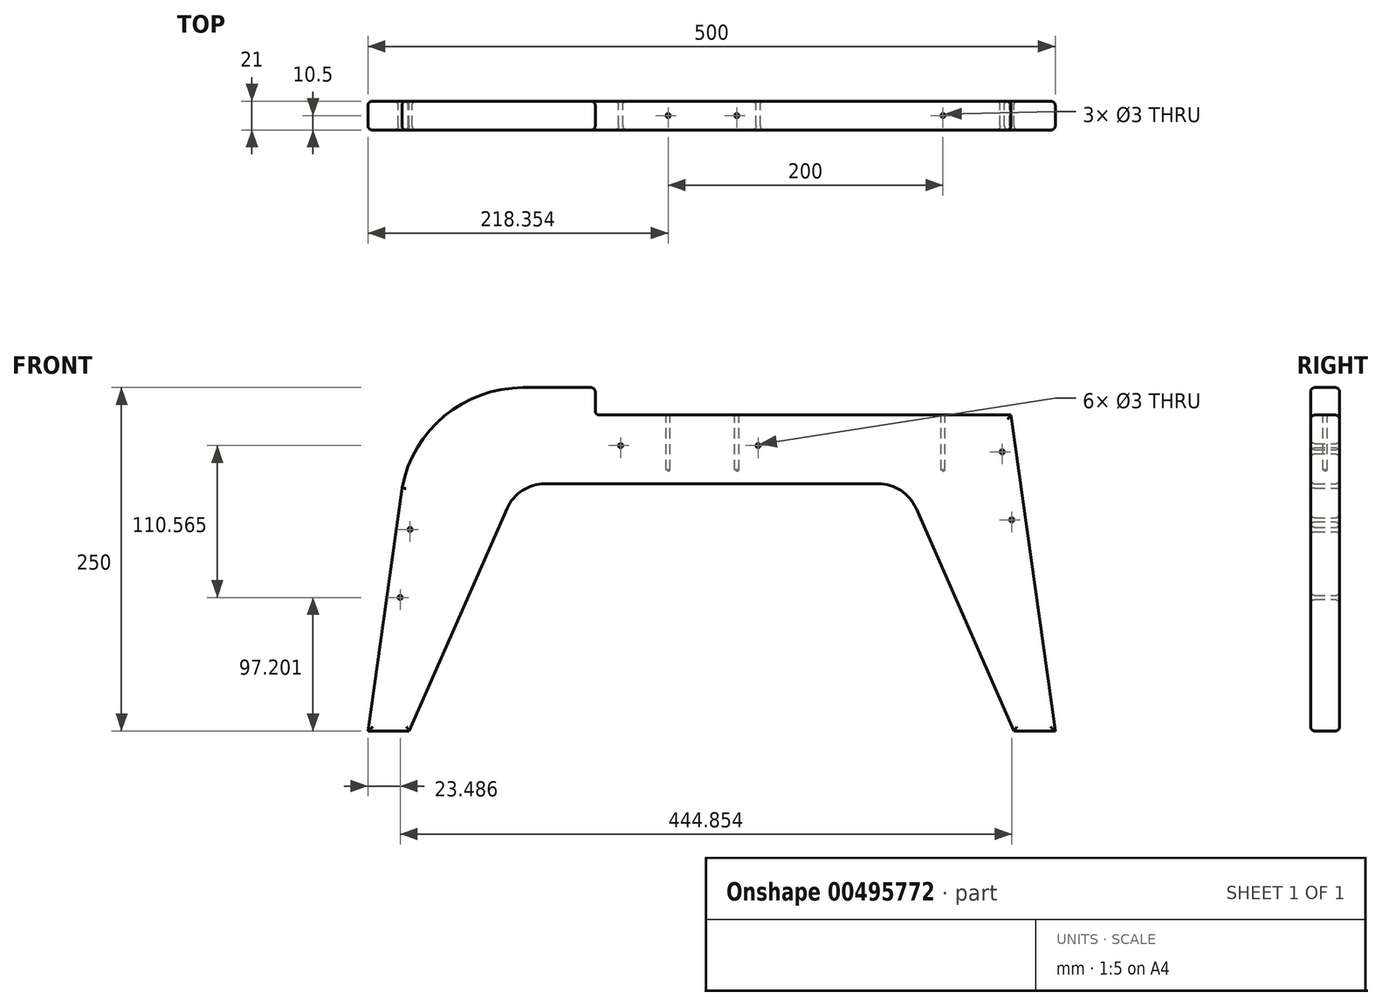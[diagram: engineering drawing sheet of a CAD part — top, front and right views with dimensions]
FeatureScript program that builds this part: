
annotation { "Feature Type Name" : "Feature", "Feature Type Description" : "" }
export const myFeature = defineFeature(function(context is Context, id is Id, definition is map)
    precondition{}
    {
        {
            var Q0;
            Q0=qCreatedBy(makeId("Front.planeOp"),FACE);
            var sketch = newSketch(context, id + "F0", { "sketchPlane" : qUnion([Q0])});
            skLineSegment(sketch, "E0.bottom", {"start": v(-250, -242.11) * mm, "end": v(-220, -242.11) * mm});
            skLineSegment(sketch, "E1", {"start": v(220, -242.11) * mm, "end": v(250, -242.11) * mm});
            skLineSegment(sketch, "E2", {"start": v(-220, -242.11) * mm, "end": v(-148.68, -80.03) * mm});
            skLineSegment(sketch, "E3", {"start": v(220, -242.11) * mm, "end": v(148.68, -80.03) * mm});
            skLineSegment(sketch, "E4", {"start": v(110, 7.89) * mm, "end": v(110, 7.89) * mm});
            skLineSegment(sketch, "E5", {"start": v(-121.22, -62.11) * mm, "end": v(121.22, -62.11) * mm});
            skLineSegment(sketch, "E6", {"start": v(217.8, -12.11) * mm, "end": v(250, -242.11) * mm});
            skPoint(sketch, "E7.end.orphan", {"position": v(110, 7.89) * mm});
            skPoint(sketch, "E8.visualSharp", {"position": v(-140.8, -62.11) * mm});
            skArc(sketch, "E8.filletArc", {"start": v(-121.22, -62.11) * mm, "mid": v(-137.62, -66.99) * mm, "end": v(-148.68, -80.03) * mm});
            skPoint(sketch, "E9.visualSharp", {"position": v(140.8, -62.11) * mm});
            skArc(sketch, "E9.filletArc", {"start": v(148.68, -80.03) * mm, "mid": v(137.62, -66.99) * mm, "end": v(121.22, -62.11) * mm});
            skLineSegment(sketch, "E10", {"start": v(-225.23, -65.16) * mm, "end": v(-250, -242.11) * mm});
            skLineSegment(sketch, "E11", {"start": v(-110, 7.89) * mm, "end": v(-137.11, 7.89) * mm});
            skArc(sketch, "E12", {"start": v(-137.11, 7.89) * mm, "mid": v(-194.34, -12.75) * mm, "end": v(-225.23, -65.16) * mm});
            skLineSegment(sketch, "E13", {"start": v(-74.6, -12.11) * mm, "end": v(217.8, -12.11) * mm});
            skLineSegment(sketch, "E14", {"start": v(-81.65, -12.11) * mm, "end": v(-74.6, -12.11) * mm});
            skLineSegment(sketch, "E15", {"start": v(-84.65, 4.89) * mm, "end": v(-84.65, -9.11) * mm});
            skLineSegment(sketch, "E16", {"start": v(-110, 7.89) * mm, "end": v(-87.65, 7.89) * mm});
            skPoint(sketch, "E17.visualSharp", {"position": v(-84.65, -12.11) * mm});
            skArc(sketch, "E17.filletArc", {"start": v(-84.65, -9.11) * mm, "mid": v(-83.77, -11.23) * mm, "end": v(-81.65, -12.11) * mm});
            skPoint(sketch, "E18.visualSharp", {"position": v(-84.65, 7.89) * mm});
            skArc(sketch, "E18.filletArc", {"start": v(-84.65, 4.89) * mm, "mid": v(-85.53, 7) * mm, "end": v(-87.65, 7.89) * mm});
            skCircle(sketch, "E19", {"center": v(-66.17, -34.35) * mm, "radius": 1.5 * mm});
            skCircle(sketch, "E20", {"center": v(33.83, -34.35) * mm, "radius": 1.5 * mm});
            skCircle(sketch, "E21", {"center": v(211.4, -38.85) * mm, "radius": 1.5 * mm});
            skCircle(sketch, "E22", {"center": v(218.34, -88.37) * mm, "radius": 1.5 * mm});
            skCircle(sketch, "E23", {"center": v(-226.51, -144.9) * mm, "radius": 1.5 * mm});
            skCircle(sketch, "E24", {"center": v(-219.37, -95.42) * mm, "radius": 1.5 * mm});
            skSolve(sketch);
        }
        {
            var Q0;
            Q0=makeQuery(id+"F0.imprint","IMPRINT",FACE,{"disambiguationData":[TD([[makeQuery(id+"F0.imprint","IMPRINT",EDGE,{"derivedFrom":sQuery(id+"F0.wireOp",EDGE,"E0.bottom")}),1.0]])]});
            extrude(context, id + "F1", {"entities" : qUnion([Q0]), "endBound" : BoundingType.SYMMETRIC, "depth" : 21 * mm});
        }
        {
            var Q0;
            Q0=makeQuery(id+"F1.opExtrude","CAP_FACE",FACE,{"disambiguationData":[OSD([sQuery(id+"F0.wireOp",EDGE,"E0.bottom"),sQuery(id+"F0.wireOp",EDGE,"E1"),sQuery(id+"F0.wireOp",EDGE,"E2"),sQuery(id+"F0.wireOp",EDGE,"E3"),sQuery(id+"F0.wireOp",EDGE,"E5"),sQuery(id+"F0.wireOp",EDGE,"E6"),sQuery(id+"F0.wireOp",EDGE,"E8.filletArc"),sQuery(id+"F0.wireOp",EDGE,"E9.filletArc"),sQuery(id+"F0.wireOp",EDGE,"E10"),sQuery(id+"F0.wireOp",EDGE,"E11"),sQuery(id+"F0.wireOp",EDGE,"E12"),sQuery(id+"F0.wireOp",EDGE,"E13"),sQuery(id+"F0.wireOp",EDGE,"E14"),sQuery(id+"F0.wireOp",EDGE,"E15"),sQuery(id+"F0.wireOp",EDGE,"E16"),sQuery(id+"F0.wireOp",EDGE,"E17.filletArc"),sQuery(id+"F0.wireOp",EDGE,"E18.filletArc"),sQuery(id+"F0.wireOp",EDGE,"E19"),sQuery(id+"F0.wireOp",EDGE,"E20"),sQuery(id+"F0.wireOp",EDGE,"E21"),sQuery(id+"F0.wireOp",EDGE,"E22"),sQuery(id+"F0.wireOp",EDGE,"E23"),sQuery(id+"F0.wireOp",EDGE,"E24")])],"isStart":false});
            var Q1;
            Q1=makeQuery(id+"F1.opExtrude","CAP_EDGE",EDGE,{"disambiguationData":[OSD([sQuery(id+"F0.wireOp",EDGE,"E2")])],"isStart":false});
            var Q2;
            Q2=makeQuery(id+"F1.opExtrude","CAP_EDGE",EDGE,{"disambiguationData":[OSD([sQuery(id+"F0.wireOp",EDGE,"E2")])],"isStart":true});
            var Q3;
            Q3=makeQuery(id+"F1.opExtrude","CAP_FACE",FACE,{"disambiguationData":[OSD([sQuery(id+"F0.wireOp",EDGE,"E0.bottom"),sQuery(id+"F0.wireOp",EDGE,"E1"),sQuery(id+"F0.wireOp",EDGE,"E2"),sQuery(id+"F0.wireOp",EDGE,"E3"),sQuery(id+"F0.wireOp",EDGE,"E5"),sQuery(id+"F0.wireOp",EDGE,"E6"),sQuery(id+"F0.wireOp",EDGE,"E8.filletArc"),sQuery(id+"F0.wireOp",EDGE,"E9.filletArc"),sQuery(id+"F0.wireOp",EDGE,"E10"),sQuery(id+"F0.wireOp",EDGE,"E11"),sQuery(id+"F0.wireOp",EDGE,"E12"),sQuery(id+"F0.wireOp",EDGE,"E13"),sQuery(id+"F0.wireOp",EDGE,"E14"),sQuery(id+"F0.wireOp",EDGE,"E15"),sQuery(id+"F0.wireOp",EDGE,"E16"),sQuery(id+"F0.wireOp",EDGE,"E17.filletArc"),sQuery(id+"F0.wireOp",EDGE,"E18.filletArc"),sQuery(id+"F0.wireOp",EDGE,"E19"),sQuery(id+"F0.wireOp",EDGE,"E20"),sQuery(id+"F0.wireOp",EDGE,"E21"),sQuery(id+"F0.wireOp",EDGE,"E22"),sQuery(id+"F0.wireOp",EDGE,"E23"),sQuery(id+"F0.wireOp",EDGE,"E24")])],"isStart":true});
            fillet(context, id + "F2", {"entities" : qUnion([Q0, Q1, Q2, Q3]), "radius" : 3 * mm, "tangentPropagation" : true, "allowEdgeOverflow" : false});
        }
        {
            var Q0;
            Q0=makeQuery(id+"F1.opExtrude","SWEPT_FACE",FACE,{"disambiguationData":[OSD([sQuery(id+"F0.wireOp",EDGE,"E13"),sQuery(id+"F0.wireOp",EDGE,"E14")])]});
            var sketch = newSketch(context, id + "F3", { "sketchPlane" : qUnion([Q0])});
            skLineSegment(sketch, "E25", {"start": v(-81.65, 0) * mm, "end": v(-31.65, 0) * mm});
            skLineSegment(sketch, "E26", {"start": v(-31.65, 0) * mm, "end": v(18.35, 0) * mm});
            skLineSegment(sketch, "E27", {"start": v(168.35, 0) * mm, "end": v(217.8, 0) * mm});
            skLineSegment(sketch, "E28", {"start": v(18.35, 0) * mm, "end": v(168.35, 0) * mm});
            skSolve(sketch);
        }
        {
            var Q0;
            Q0=sQuery(id+"F3.wireOp",VERTEX,"E26.start");
            var Q1;
            Q1=makeQuery(id+"F1.opExtrude","SWEPT_BODY",BODY,{"disambiguationData":[OSD([sQuery(id+"F0.wireOp",EDGE,"E0.bottom"),sQuery(id+"F0.wireOp",EDGE,"E1"),sQuery(id+"F0.wireOp",EDGE,"E2"),sQuery(id+"F0.wireOp",EDGE,"E3"),sQuery(id+"F0.wireOp",EDGE,"E5"),sQuery(id+"F0.wireOp",EDGE,"E6"),sQuery(id+"F0.wireOp",EDGE,"E8.filletArc"),sQuery(id+"F0.wireOp",EDGE,"E9.filletArc"),sQuery(id+"F0.wireOp",EDGE,"E10"),sQuery(id+"F0.wireOp",EDGE,"E11"),sQuery(id+"F0.wireOp",EDGE,"E12"),sQuery(id+"F0.wireOp",EDGE,"E13"),sQuery(id+"F0.wireOp",EDGE,"E14"),sQuery(id+"F0.wireOp",EDGE,"E15"),sQuery(id+"F0.wireOp",EDGE,"E16"),sQuery(id+"F0.wireOp",EDGE,"E17.filletArc"),sQuery(id+"F0.wireOp",EDGE,"E18.filletArc"),sQuery(id+"F0.wireOp",EDGE,"E19"),sQuery(id+"F0.wireOp",EDGE,"E20"),sQuery(id+"F0.wireOp",EDGE,"E21"),sQuery(id+"F0.wireOp",EDGE,"E22"),sQuery(id+"F0.wireOp",EDGE,"E23"),sQuery(id+"F0.wireOp",EDGE,"E24")])]});
            hole(context, id + "F4", {"style" : HoleStyle.SIMPLE, "endStyle" : HoleEndStyle.BLIND, "holeDiameter" : 3 * mm, "holeDepth" : 40 * mm, "isTappedThrough" : true, "tappedDepth" : 12 * mm, "tapClearance" : 3, "locations" : qUnion([Q0]), "scope" : qUnion([Q1])});
        }
        {
            var Q0;
            Q0=sQuery(id+"F3.wireOp",VERTEX,"E28.start");
            var Q1;
            Q1=makeQuery(id+"F1.opExtrude","SWEPT_BODY",BODY,{"disambiguationData":[OSD([sQuery(id+"F0.wireOp",EDGE,"E0.bottom"),sQuery(id+"F0.wireOp",EDGE,"E1"),sQuery(id+"F0.wireOp",EDGE,"E2"),sQuery(id+"F0.wireOp",EDGE,"E3"),sQuery(id+"F0.wireOp",EDGE,"E5"),sQuery(id+"F0.wireOp",EDGE,"E6"),sQuery(id+"F0.wireOp",EDGE,"E8.filletArc"),sQuery(id+"F0.wireOp",EDGE,"E9.filletArc"),sQuery(id+"F0.wireOp",EDGE,"E10"),sQuery(id+"F0.wireOp",EDGE,"E11"),sQuery(id+"F0.wireOp",EDGE,"E12"),sQuery(id+"F0.wireOp",EDGE,"E13"),sQuery(id+"F0.wireOp",EDGE,"E14"),sQuery(id+"F0.wireOp",EDGE,"E15"),sQuery(id+"F0.wireOp",EDGE,"E16"),sQuery(id+"F0.wireOp",EDGE,"E17.filletArc"),sQuery(id+"F0.wireOp",EDGE,"E18.filletArc"),sQuery(id+"F0.wireOp",EDGE,"E19"),sQuery(id+"F0.wireOp",EDGE,"E20"),sQuery(id+"F0.wireOp",EDGE,"E21"),sQuery(id+"F0.wireOp",EDGE,"E22"),sQuery(id+"F0.wireOp",EDGE,"E23"),sQuery(id+"F0.wireOp",EDGE,"E24")])]});
            hole(context, id + "F5", {"style" : HoleStyle.SIMPLE, "endStyle" : HoleEndStyle.BLIND, "holeDiameter" : 3 * mm, "holeDepth" : 40 * mm, "isTappedThrough" : true, "tappedDepth" : 12 * mm, "tapClearance" : 3, "locations" : qUnion([Q0]), "scope" : qUnion([Q1])});
        }
        {
            var Q0;
            Q0=sQuery(id+"F3.wireOp",VERTEX,"E28.end");
            var Q1;
            Q1=makeQuery(id+"F1.opExtrude","SWEPT_BODY",BODY,{"disambiguationData":[OSD([sQuery(id+"F0.wireOp",EDGE,"E0.bottom"),sQuery(id+"F0.wireOp",EDGE,"E1"),sQuery(id+"F0.wireOp",EDGE,"E2"),sQuery(id+"F0.wireOp",EDGE,"E3"),sQuery(id+"F0.wireOp",EDGE,"E5"),sQuery(id+"F0.wireOp",EDGE,"E6"),sQuery(id+"F0.wireOp",EDGE,"E8.filletArc"),sQuery(id+"F0.wireOp",EDGE,"E9.filletArc"),sQuery(id+"F0.wireOp",EDGE,"E10"),sQuery(id+"F0.wireOp",EDGE,"E11"),sQuery(id+"F0.wireOp",EDGE,"E12"),sQuery(id+"F0.wireOp",EDGE,"E13"),sQuery(id+"F0.wireOp",EDGE,"E14"),sQuery(id+"F0.wireOp",EDGE,"E15"),sQuery(id+"F0.wireOp",EDGE,"E16"),sQuery(id+"F0.wireOp",EDGE,"E17.filletArc"),sQuery(id+"F0.wireOp",EDGE,"E18.filletArc"),sQuery(id+"F0.wireOp",EDGE,"E19"),sQuery(id+"F0.wireOp",EDGE,"E20"),sQuery(id+"F0.wireOp",EDGE,"E21"),sQuery(id+"F0.wireOp",EDGE,"E22"),sQuery(id+"F0.wireOp",EDGE,"E23"),sQuery(id+"F0.wireOp",EDGE,"E24")])]});
            hole(context, id + "F6", {"style" : HoleStyle.SIMPLE, "endStyle" : HoleEndStyle.BLIND, "holeDiameter" : 3 * mm, "holeDepth" : 40 * mm, "isTappedThrough" : true, "tappedDepth" : 12 * mm, "tapClearance" : 3, "locations" : qUnion([Q0]), "scope" : qUnion([Q1])});
        }
    });
